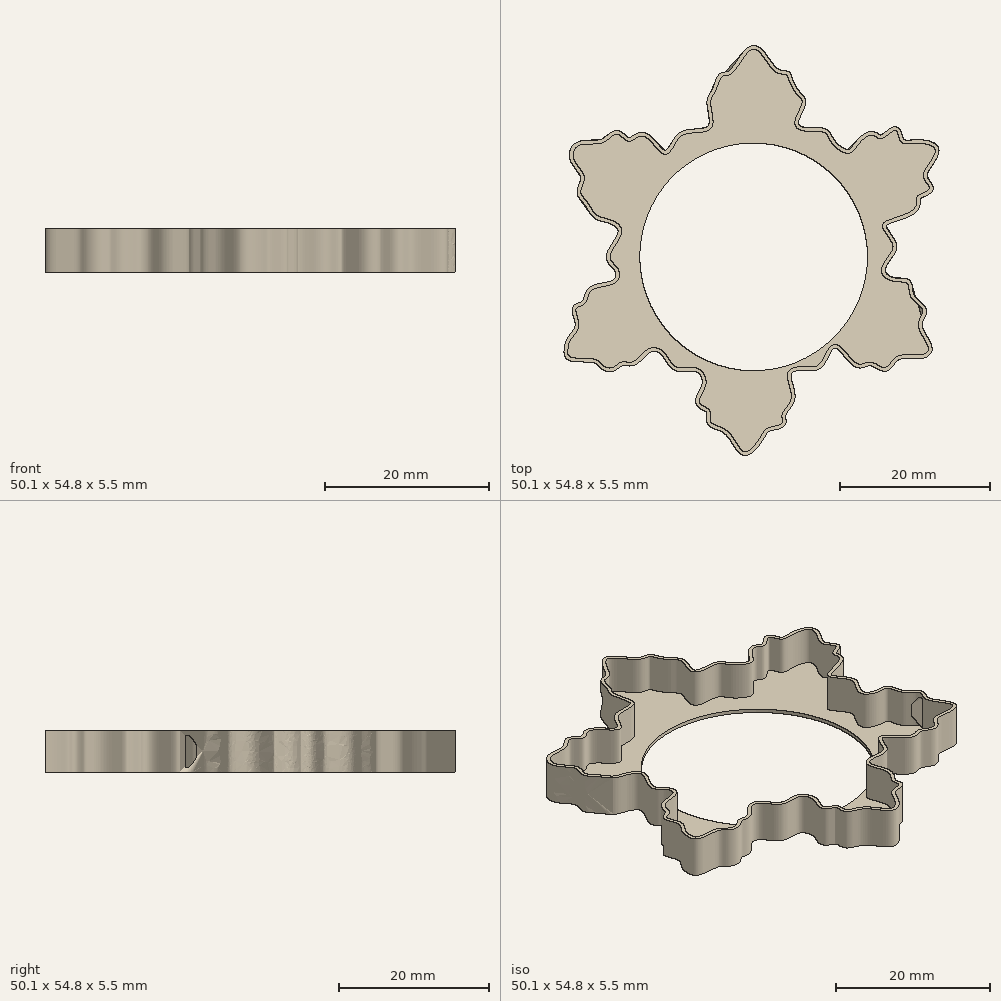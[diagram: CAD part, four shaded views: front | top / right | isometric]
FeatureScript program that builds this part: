
annotation { "Feature Type Name" : "Feature", "Feature Type Description" : "" }
export const myFeature = defineFeature(function(context is Context, id is Id, definition is map)
    precondition{}
    {
        {
            var Q0;
            Q0=qCreatedBy(makeId("Top.planeOp"),FACE);
            var sketch = newSketch(context, id + "F0", { "sketchPlane" : qUnion([Q0])});
            skFitSpline(sketch, "E0", {"points": [v(0, 55.55) * mm, v(-5.87, 48.94) * mm, v(-8.32, 48.21) * mm, v(-10.28, 44.05) * mm, v(-11.5, 41.36) * mm, v(-11.25, 34.5) * mm, v(-17.37, 33.04) * mm, v(-20.55, 30.84) * mm, v(-23.73, 27.41) * mm, v(-29.6, 32.3) * mm, v(-33.27, 30.84) * mm, v(-36.45, 32.8) * mm, v(-40.12, 30.6) * mm, v(-46.49, 29.86) * mm, v(-48.2, 26.44) * mm, v(-45.26, 21.3) * mm, v(-46.24, 17.38) * mm, v(-44.53, 14.7) * mm, v(-42.08, 11.27) * mm, v(-38.66, 10.04) * mm, v(-35.23, 6.86) * mm, v(-38.41, 0) * mm, v(-36.45, -2.92) * mm, v(-36.45, -6.6) * mm, v(-41.84, -8.3) * mm, v(-44.04, -10.02) * mm, v(-45.26, -12.7) * mm, v(-47.46, -13.93) * mm, v(-46.73, -18.34) * mm, v(-48.93, -22.25) * mm, v(-49.67, -24.7) * mm, v(-49.18, -26.66) * mm, v(-42.33, -27.39) * mm, v(-40.12, -29.1) * mm, v(-37.68, -29.6) * mm, v(-35.23, -28.12) * mm, v(-32.54, -28.12) * mm, v(-29.85, -26.17) * mm, v(-27.65, -24.45) * mm, v(-24.22, -25.19) * mm, v(-20.8, -29.35) * mm, v(-14.92, -29.84) * mm, v(-12.72, -33.75) * mm, v(-14.2, -37.42) * mm, v(-14.2, -39.38) * mm, v(-11.74, -41.1) * mm, v(-11.5, -44.03) * mm, v(-8.32, -45.74) * mm, v(-5.14, -48.92) * mm, v(-2.2, -52.1) * mm, v(1.71, -48.43) * mm, v(3.91, -45.74) * mm, v(7.58, -44.52) * mm, v(7.58, -42.31) * mm, v(10.03, -37.91) * mm, v(9.05, -31.3) * mm, v(12.48, -29.35) * mm, v(17.13, -29.1) * mm, v(19.57, -25.43) * mm, v(22.26, -23.48) * mm, v(27.9, -28.61) * mm, v(31.32, -28.12) * mm, v(35.23, -29.6) * mm, v(38.41, -26.66) * mm, v(45.02, -26.17) * mm, v(46.73, -24.45) * mm, v(44.04, -18.1) * mm, v(45.26, -14.42) * mm, v(42.08, -10.75) * mm, v(41.1, -7.08) * mm, v(37.68, -6.6) * mm, v(34.25, -4.15) * mm, v(35.97, 0) * mm, v(37.19, 3.2) * mm, v(34.5, 7.84) * mm, v(35.48, 9.55) * mm, v(41.84, 12) * mm, v(43.55, 14.2) * mm, v(43.8, 16.16) * mm, v(46.98, 18.12) * mm, v(45.5, 21.05) * mm, v(46.98, 24.97) * mm, v(48.44, 28.88) * mm, v(43.8, 30.35) * mm, v(39.4, 30.84) * mm, v(37.92, 33.78) * mm, v(34.25, 31.57) * mm, v(31.8, 32.55) * mm, v(28.14, 30.1) * mm, v(25.45, 27.66) * mm, v(20.8, 30.6) * mm, v(18.84, 33.29) * mm, v(12.97, 33.78) * mm, v(11.01, 35.98) * mm, v(12.97, 41.36) * mm, v(11.5, 43.56) * mm, v(9.3, 47.72) * mm, v(8.8, 48.7) * mm, v(5.63, 49.68) * mm, v(0, 55.55) * mm]});
            skSolve(sketch);
        }
        {
            var Q0;
            Q0=makeQuery(id+"F0.imprint","IMPRINT",FACE,{"disambiguationData":[TD([[makeQuery(id+"F0.imprint","IMPRINT",EDGE,{"derivedFrom":sQuery(id+"F0.wireOp",EDGE,"E0")}),1.0]])]});
            extrude(context, id + "F1", {"entities" : qUnion([Q0]), "depth" : 10 * mm});
        }
        {
            var Q0;
            Q0=makeQuery(id+"F1.opExtrude","CAP_FACE",FACE,{"disambiguationData":[OSD([sQuery(id+"F0.wireOp",EDGE,"E0")])],"isStart":false});
            shell(context, id + "F2", {"entities" : qUnion([Q0]), "thickness" : 1 * mm, "oppositeDirection" : true});
        }
        {
            var Q0;
            {var subQ0=sQuery(id+"F0.wireOp",EDGE,"E0");Q0=makeQuery(id+"F2.opShell","OFFSET_FACE",FACE,{"disambiguationData":[OSD([subQ0]),TDD([makeQuery(id+"F1.opExtrude","CAP_FACE",FACE,{"disambiguationData":[OSD([subQ0])],"isStart":true})])]});}
            var sketch = newSketch(context, id + "F3", { "sketchPlane" : qUnion([Q0])});
            skCircle(sketch, "E1", {"center": v(0, 0) * mm, "radius": 30.45 * mm});
            skSolve(sketch);
        }
        {
            var Q0;
            Q0=qSketchRegion(id+"F3",true);
            extrude(context, id + "F4", {"entities" : qUnion([Q0]), "operationType" : NewBodyOperationType.REMOVE, "oppositeDirection" : true, "depth" : 25 * mm});
        }
        {
            var Q0;
            Q0=makeQuery(id+"F1.opExtrude","SWEPT_BODY",BODY,{"disambiguationData":[OSD([sQuery(id+"F0.wireOp",EDGE,"E0")])]});
            var Q1;
            Q1=qCreatedBy(makeId("Origin.pointOp"),VERTEX);
            transform(context, id + "F5", {"entities" : qUnion([Q0]), "transformType" : TransformType.SCALE_UNIFORMLY, "scale" : 0.5, "scalePoint" : qUnion([Q1]), "makeCopy" : false});
        }
    });
